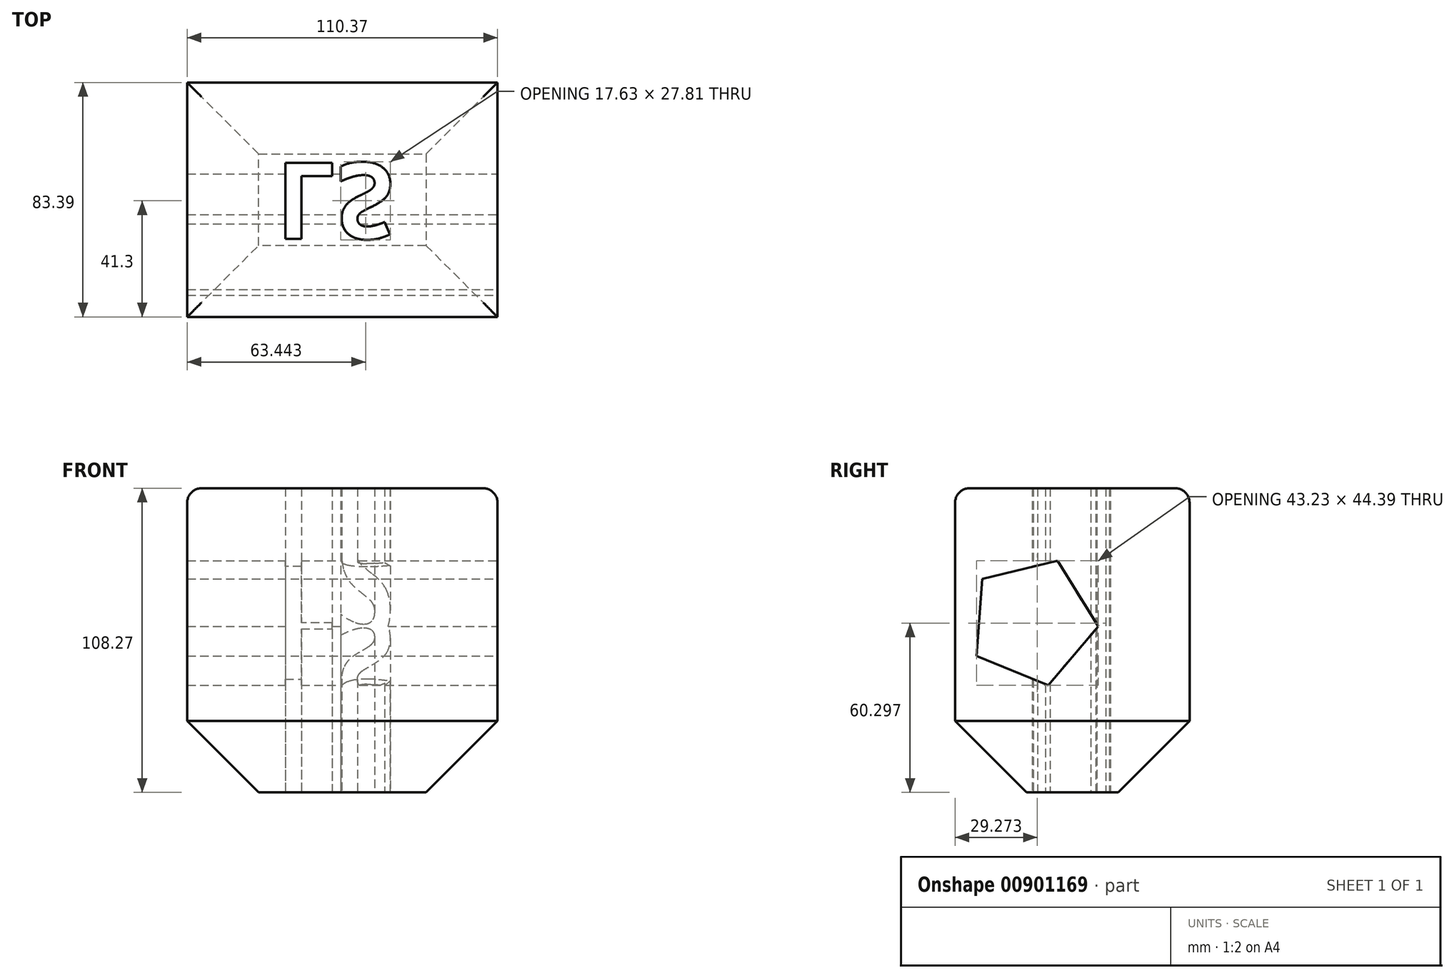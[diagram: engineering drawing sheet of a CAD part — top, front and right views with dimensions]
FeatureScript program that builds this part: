
annotation { "Feature Type Name" : "Feature", "Feature Type Description" : "" }
export const myFeature = defineFeature(function(context is Context, id is Id, definition is map)
    precondition{}
    {
        {
            var Q0;
            Q0=qCreatedBy(makeId("Top.planeOp"),FACE);
            var sketch = newSketch(context, id + "F0", { "sketchPlane" : qUnion([Q0])});
            skLineSegment(sketch, "E0.bottom", {"start": v(-52.94, -27.55) * mm, "end": v(57.43, -27.55) * mm});
            skLineSegment(sketch, "E0.top", {"start": v(-52.94, 55.84) * mm, "end": v(57.43, 55.84) * mm});
            skLineSegment(sketch, "E0.left", {"start": v(-52.94, -27.55) * mm, "end": v(-52.94, 55.84) * mm});
            skLineSegment(sketch, "E0.right", {"start": v(57.43, -27.55) * mm, "end": v(57.43, 55.84) * mm});
            skSolve(sketch);
        }
        {
            var Q0;
            Q0 = qSketchRegion(id + "F0", true);
            extrude(context, id + "F1", {"entities" : qUnion([Q0]), "depth" : 108.27 * mm, "offsetDistance" : 25.4 * mm});
        }
        {
            var Q0;
            Q0=makeQuery(id+"F1.opExtrude","CAP_EDGE",EDGE,{"disambiguationData":[OSD([sQuery(id+"F0.wireOp",EDGE,"E0.bottom")])],"isStart":false});
            var Q1;
            Q1=makeQuery(id+"F1.opExtrude","CAP_EDGE",EDGE,{"disambiguationData":[OSD([sQuery(id+"F0.wireOp",EDGE,"E0.top")])],"isStart":false});
            var Q2;
            Q2=makeQuery(id+"F1.opExtrude","CAP_EDGE",EDGE,{"disambiguationData":[OSD([sQuery(id+"F0.wireOp",EDGE,"E0.right")])],"isStart":false});
            var Q3;
            Q3=makeQuery(id+"F1.opExtrude","CAP_EDGE",EDGE,{"disambiguationData":[OSD([sQuery(id+"F0.wireOp",EDGE,"E0.left")])],"isStart":false});
            fillet(context, id + "F2", {"entities" : qUnion([Q0, Q1, Q2, Q3]), "radius" : 5.08 * mm, "tangentPropagation" : true, "allowEdgeOverflow" : false});
        }
        {
            var Q0;
            Q0=makeQuery(id+"F1.opExtrude","CAP_FACE",FACE,{"disambiguationData":[OSD([sQuery(id+"F0.wireOp",EDGE,"E0.bottom"),sQuery(id+"F0.wireOp",EDGE,"E0.top"),sQuery(id+"F0.wireOp",EDGE,"E0.left"),sQuery(id+"F0.wireOp",EDGE,"E0.right")])],"isStart":true});
            var sketch = newSketch(context, id + "F3", { "sketchPlane" : qUnion([Q0])});
            skText(sketch, "E1", { "text": "LS", "fontName": "OpenSans-Bold.ttf"});
            const initialGuessF3  = {"E1": [-0.02146, -0.02728, 1, 0, 0.02728]};
            skSetInitialGuess(sketch, initialGuessF3);
            skSolve(sketch);
        }
        {
            var Q0;
            Q0 = qSketchRegion(id + "F3", true);
            extrude(context, id + "F4", {"entities" : qUnion([Q0]), "operationType" : NewBodyOperationType.REMOVE, "oppositeDirection" : true, "depth" : 254 * mm, "offsetDistance" : 25.4 * mm});
        }
        {
            var Q0;
            Q0=makeQuery(id+"F1.opExtrude","CAP_EDGE",EDGE,{"disambiguationData":[OSD([sQuery(id+"F0.wireOp",EDGE,"E0.right")])],"isStart":true});
            var Q1;
            Q1=makeQuery(id+"F1.opExtrude","CAP_EDGE",EDGE,{"disambiguationData":[OSD([sQuery(id+"F0.wireOp",EDGE,"E0.top")])],"isStart":true});
            var Q2;
            Q2=makeQuery(id+"F1.opExtrude","CAP_EDGE",EDGE,{"disambiguationData":[OSD([sQuery(id+"F0.wireOp",EDGE,"E0.bottom")])],"isStart":true});
            var Q3;
            Q3=makeQuery(id+"F1.opExtrude","CAP_EDGE",EDGE,{"disambiguationData":[OSD([sQuery(id+"F0.wireOp",EDGE,"E0.left")])],"isStart":true});
            chamfer(context, id + "F5", {"entities" : qUnion([Q0, Q1, Q2, Q3]), "width" : 25.4 * mm, "tangentPropagation" : true});
        }
        {
            var Q0;
            Q0=makeQuery(id+"F1.opExtrude","SWEPT_FACE",FACE,{"disambiguationData":[OSD([sQuery(id+"F0.wireOp",EDGE,"E0.right")])]});
            var sketch = newSketch(context, id + "F6", { "sketchPlane" : qUnion([Q0])});
            skCircle(sketch, "E2.cCircle", {"center": v(0, 60.83) * mm, "radius": 18.93 * mm, "construction": true});
            skLineSegment(sketch, "E2.0", {"start": v(8.85, 82.5) * mm, "end": v(23.34, 59.1) * mm});
            skLineSegment(sketch, "E2.1", {"start": v(23.34, 59.1) * mm, "end": v(5.58, 38.1) * mm});
            skLineSegment(sketch, "E2.2", {"start": v(5.58, 38.1) * mm, "end": v(-19.89, 48.5) * mm});
            skLineSegment(sketch, "E2.3", {"start": v(-19.89, 48.5) * mm, "end": v(-17.87, 75.94) * mm});
            skLineSegment(sketch, "E2.4", {"start": v(-17.87, 75.94) * mm, "end": v(8.85, 82.5) * mm});
            skPoint(sketch, "E2.0.midPoint", {"position": v(16.1, 70.8) * mm});
            skSolve(sketch);
        }
        {
            var Q0;
            Q0=makeQuery(id+"F6.imprint","IMPRINT",FACE,{"disambiguationData":[TD([[makeQuery(id+"F6.imprint","IMPRINT",EDGE,{"derivedFrom":sQuery(id+"F6.wireOp",EDGE,"E2.0")}),-1.0]])]});
            extrude(context, id + "F7", {"entities" : qUnion([Q0]), "operationType" : NewBodyOperationType.REMOVE, "oppositeDirection" : true, "depth" : 127 * mm, "offsetDistance" : 25.4 * mm});
        }
    });
